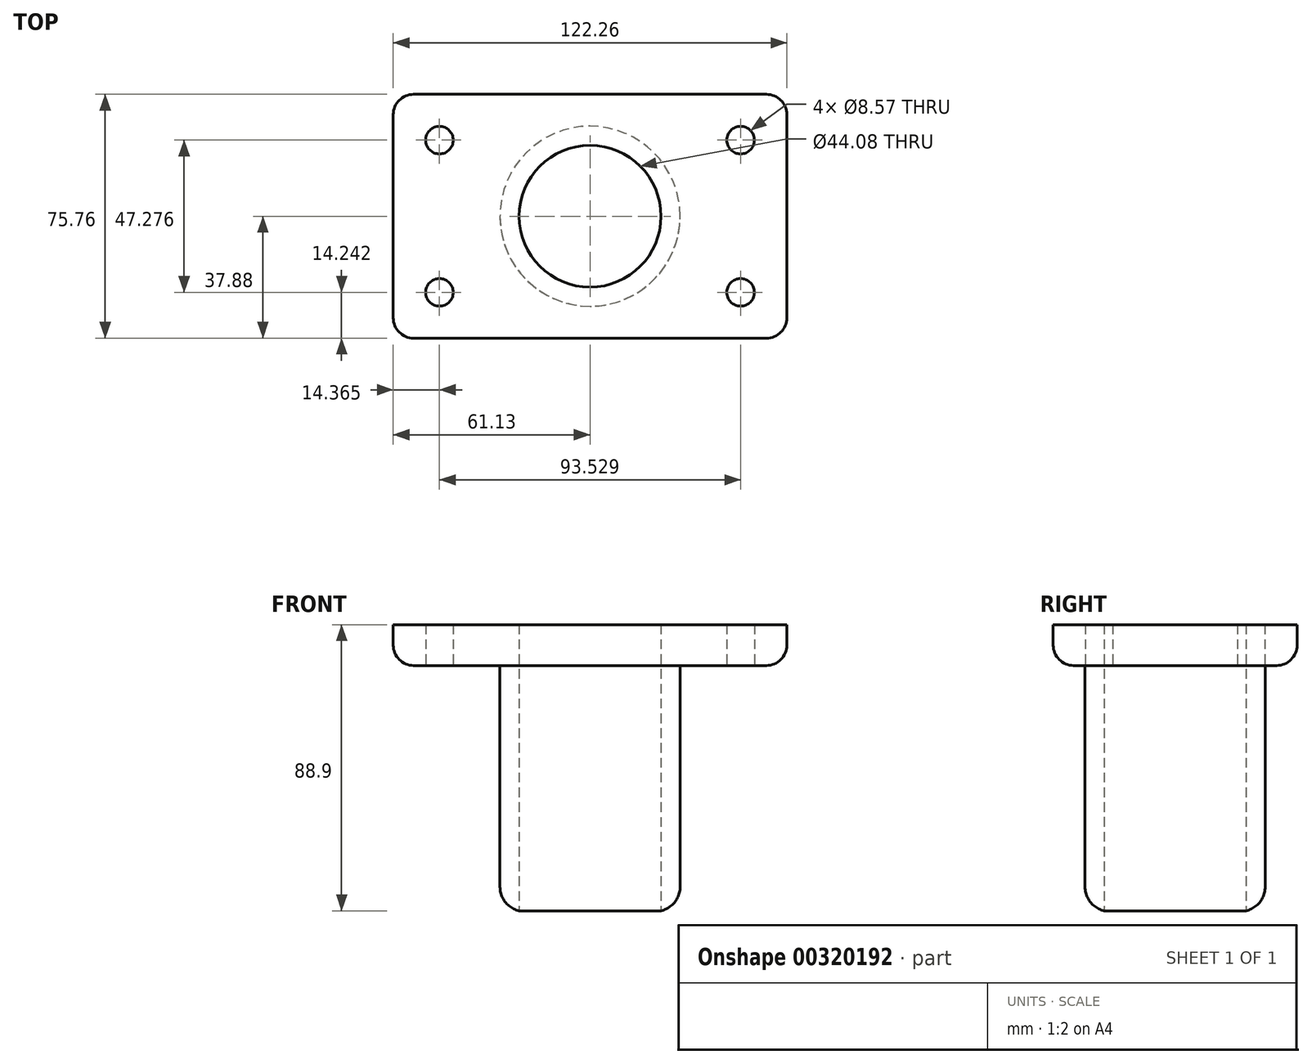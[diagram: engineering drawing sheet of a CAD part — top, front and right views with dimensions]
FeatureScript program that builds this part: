
annotation { "Feature Type Name" : "Feature", "Feature Type Description" : "" }
export const myFeature = defineFeature(function(context is Context, id is Id, definition is map)
    precondition{}
    {
        {
            var Q0;
            Q0=qCreatedBy(makeId("Top.planeOp"),FACE);
            var sketch = newSketch(context, id + "F0", { "sketchPlane" : qUnion([Q0])});
            skCircle(sketch, "E0", {"center": v(0, 0) * mm, "radius": 22.04 * mm});
            skCircle(sketch, "E1", {"center": v(0, 0) * mm, "radius": 27.97 * mm});
            skSolve(sketch);
        }
        {
            var Q0;
            Q0=makeQuery(id+"F0.imprint","IMPRINT",FACE,{"disambiguationData":[TD([[makeQuery(id+"F0.imprint","IMPRINT",EDGE,{"derivedFrom":sQuery(id+"F0.wireOp",EDGE,"E0")}),-1.0]])]});
            extrude(context, id + "F1", {"entities" : qUnion([Q0]), "depth" : 76.2 * mm});
        }
        {
            var Q0;
            Q0=makeQuery(id+"F1.opExtrude","CAP_FACE",FACE,{"disambiguationData":[OSD([sQuery(id+"F0.wireOp",EDGE,"E0"),sQuery(id+"F0.wireOp",EDGE,"E1")])],"isStart":false});
            var sketch = newSketch(context, id + "F2", { "sketchPlane" : qUnion([Q0])});
            skLineSegment(sketch, "E2.bottom", {"start": v(54.78, -37.88) * mm, "end": v(-54.78, -37.88) * mm});
            skLineSegment(sketch, "E2.top", {"start": v(54.78, 37.88) * mm, "end": v(-54.78, 37.88) * mm});
            skLineSegment(sketch, "E2.left", {"start": v(61.13, -31.53) * mm, "end": v(61.13, 31.53) * mm});
            skLineSegment(sketch, "E2.right", {"start": v(-61.13, -31.53) * mm, "end": v(-61.13, 31.53) * mm});
            skPoint(sketch, "E2.middle", {"position": v(0, 0) * mm});
            skPoint(sketch, "E3.visualSharp", {"position": v(-61.13, -37.88) * mm});
            skArc(sketch, "E3.filletArc", {"start": v(-61.13, -31.53) * mm, "mid": v(-59.27, -36.02) * mm, "end": v(-54.78, -37.88) * mm});
            skPoint(sketch, "E4.visualSharp", {"position": v(61.13, -37.88) * mm});
            skArc(sketch, "E4.filletArc", {"start": v(54.78, -37.88) * mm, "mid": v(59.27, -36.02) * mm, "end": v(61.13, -31.53) * mm});
            skPoint(sketch, "E5.visualSharp", {"position": v(61.13, 37.88) * mm});
            skArc(sketch, "E5.filletArc", {"start": v(61.13, 31.53) * mm, "mid": v(59.27, 36.02) * mm, "end": v(54.78, 37.88) * mm});
            skPoint(sketch, "E6.visualSharp", {"position": v(-61.13, 37.88) * mm});
            skArc(sketch, "E6.filletArc", {"start": v(-54.78, 37.88) * mm, "mid": v(-59.27, 36.02) * mm, "end": v(-61.13, 31.53) * mm});
            skSolve(sketch);
        }
        {
            var Q0;
            Q0 = qSketchRegion(id + "F2", true);
            extrude(context, id + "F3", {"entities" : qUnion([Q0]), "operationType" : NewBodyOperationType.ADD, "depth" : 12.7 * mm});
        }
        {
            var Q0;
            Q0=makeQuery(id+"F1.opExtrude","CAP_EDGE",EDGE,{"disambiguationData":[OSD([sQuery(id+"F0.wireOp",EDGE,"E1")])],"isStart":true});
            fillet(context, id + "F4", {"entities" : qUnion([Q0]), "radius" : 7.62 * mm, "tangentPropagation" : true, "allowEdgeOverflow" : false});
        }
        {
            var Q0;
            Q0=makeQuery(id+"F3.opExtrude","CAP_EDGE",EDGE,{"disambiguationData":[OSD([sQuery(id+"F2.wireOp",EDGE,"E2.right")])],"isStart":true});
            var Q1;
            Q1=makeQuery(id+"F3.opExtrude","CAP_EDGE",EDGE,{"disambiguationData":[OSD([sQuery(id+"F2.wireOp",EDGE,"E2.bottom")])],"isStart":true});
            var Q2;
            Q2=makeQuery(id+"F3.opExtrude","CAP_EDGE",EDGE,{"disambiguationData":[OSD([sQuery(id+"F2.wireOp",EDGE,"E2.left")])],"isStart":true});
            var Q3;
            Q3=makeQuery(id+"F3.opExtrude","CAP_EDGE",EDGE,{"disambiguationData":[OSD([sQuery(id+"F2.wireOp",EDGE,"E2.top")])],"isStart":true});
            fillet(context, id + "F5", {"entities" : qUnion([Q0, Q1, Q2, Q3]), "radius" : 6.35 * mm, "tangentPropagation" : true, "allowEdgeOverflow" : false});
        }
        {
            var Q0;
            {var subQ0=sQuery(id+"F2.wireOp",EDGE,"E2.left");var subQ1=sQuery(id+"F2.wireOp",EDGE,"E2.top");var subQ2=sQuery(id+"F2.wireOp",EDGE,"E2.bottom");var subQ3=sQuery(id+"F2.wireOp",EDGE,"E2.right");var subQ4=sQuery(id+"F2.wireOp",EDGE,"E3.filletArc");var subQ5=sQuery(id+"F2.wireOp",EDGE,"E4.filletArc");var subQ6=sQuery(id+"F2.wireOp",EDGE,"E5.filletArc");var subQ7=sQuery(id+"F2.wireOp",EDGE,"E6.filletArc");Q0=makeQuery(id+"F3.boolean.opBoolean","SPLIT",FACE,{"disambiguationData":[TD([makeQuery(id+"F1.opExtrude","SWEPT_FACE",FACE,{"disambiguationData":[OSD([sQuery(id+"F0.wireOp",EDGE,"E1")])]})])],"derivedFrom":makeQuery(id+"F3.opExtrude","CAP_FACE",FACE,{"disambiguationData":[OSD([subQ2,subQ1,subQ0,subQ3,subQ4,subQ5,subQ6,subQ7])],"isStart":true})});}
            var sketch = newSketch(context, id + "F6", { "sketchPlane" : qUnion([Q0])});
            skCircle(sketch, "E7", {"center": v(46.76, -23.64) * mm, "radius": 4.28 * mm});
            skCircle(sketch, "E8.MirrorC", {"center": v(-46.76, -23.64) * mm, "radius": 4.28 * mm});
            skCircle(sketch, "E9.MirrorC", {"center": v(46.76, 23.64) * mm, "radius": 4.28 * mm});
            skCircle(sketch, "E10.MirrorC", {"center": v(-46.76, 23.64) * mm, "radius": 4.28 * mm});
            skSolve(sketch);
        }
        {
            var Q0;
            Q0 = qSketchRegion(id + "F6", true);
            extrude(context, id + "F7", {"entities" : qUnion([Q0]), "operationType" : NewBodyOperationType.REMOVE, "oppositeDirection" : true, "depth" : 25.4 * mm});
        }
        {
            var Q0;
            Q0=makeQuery(id+"F3.boolean.opBoolean","SPLIT",FACE,{"disambiguationData":[TD([makeQuery(id+"F1.opExtrude","SWEPT_FACE",FACE,{"disambiguationData":[OSD([sQuery(id+"F0.wireOp",EDGE,"E0")])]})])],"derivedFrom":makeQuery(id+"F3.opExtrude","CAP_FACE",FACE,{"disambiguationData":[OSD([sQuery(id+"F2.wireOp",EDGE,"E2.bottom"),sQuery(id+"F2.wireOp",EDGE,"E2.top"),sQuery(id+"F2.wireOp",EDGE,"E2.left"),sQuery(id+"F2.wireOp",EDGE,"E2.right"),sQuery(id+"F2.wireOp",EDGE,"E3.filletArc"),sQuery(id+"F2.wireOp",EDGE,"E4.filletArc"),sQuery(id+"F2.wireOp",EDGE,"E5.filletArc"),sQuery(id+"F2.wireOp",EDGE,"E6.filletArc")])],"isStart":true})});
            extrude(context, id + "F8", {"entities" : qUnion([Q0]), "operationType" : NewBodyOperationType.REMOVE, "oppositeDirection" : true, "depth" : 25.4 * mm});
        }
    });
